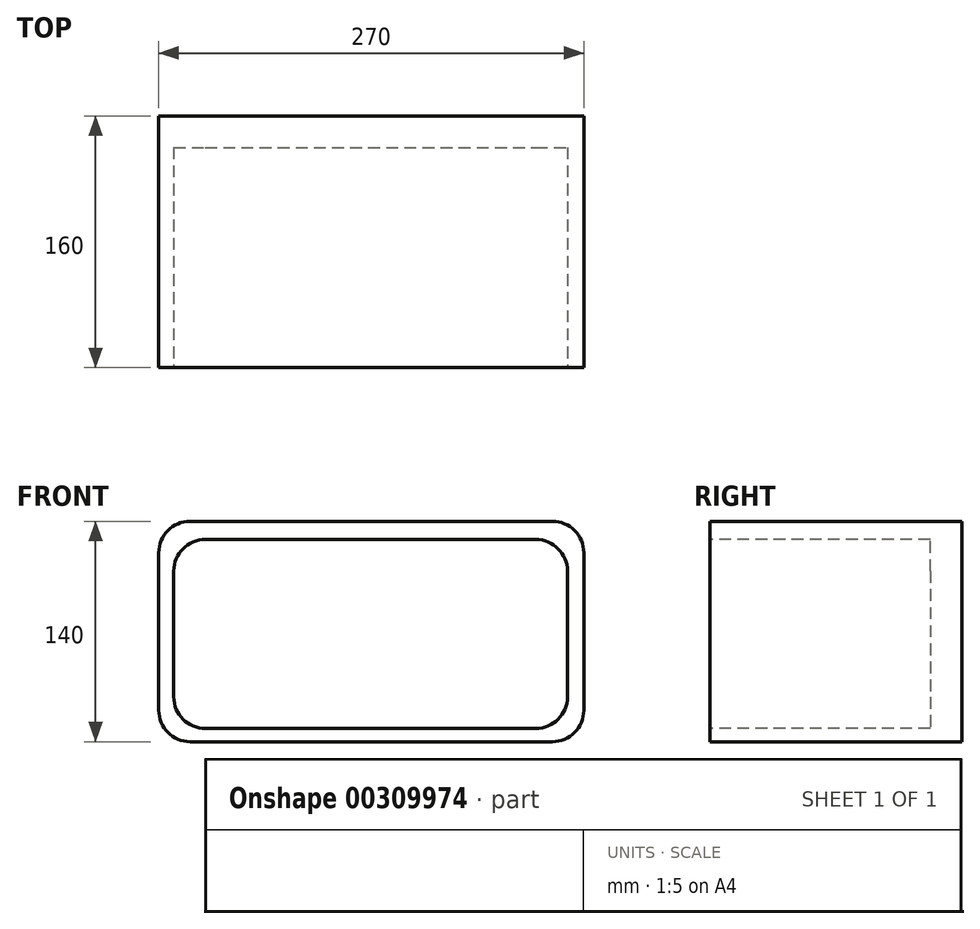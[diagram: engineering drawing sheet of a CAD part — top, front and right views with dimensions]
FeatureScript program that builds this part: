
annotation { "Feature Type Name" : "Feature", "Feature Type Description" : "" }
export const myFeature = defineFeature(function(context is Context, id is Id, definition is map)
    precondition{}
    {
        {
            var Q0;
            Q0=qCreatedBy(makeId("Front.planeOp"),FACE);
            var sketch = newSketch(context, id + "F0", { "sketchPlane" : qUnion([Q0])});
            skLineSegment(sketch, "E0.bottom", {"start": v(-135, 70) * mm, "end": v(135, 70) * mm});
            skLineSegment(sketch, "E0.top", {"start": v(-135, -70) * mm, "end": v(135, -70) * mm});
            skLineSegment(sketch, "E0.left", {"start": v(-135, 70) * mm, "end": v(-135, -70) * mm});
            skLineSegment(sketch, "E0.right", {"start": v(135, 70) * mm, "end": v(135, -70) * mm});
            skPoint(sketch, "E0.middle", {"position": v(0, 0) * mm});
            skSolve(sketch);
        }
        {
            var Q0;
            Q0 = qSketchRegion(id + "F0", true);
            extrude(context, id + "F1", {"entities" : qUnion([Q0]), "depth" : 160 * mm});
        }
        {
            var Q0;
            Q0=makeQuery(id+"F1.opExtrude","CAP_FACE",FACE,{"disambiguationData":[OSD([sQuery(id+"F0.wireOp",EDGE,"E0.bottom"),sQuery(id+"F0.wireOp",EDGE,"E0.top"),sQuery(id+"F0.wireOp",EDGE,"E0.left"),sQuery(id+"F0.wireOp",EDGE,"E0.right")])],"isStart":false});
            var sketch = newSketch(context, id + "F2", { "sketchPlane" : qUnion([Q0])});
            skLineSegment(sketch, "E1.bottom", {"start": v(-125.42, 58.4) * mm, "end": v(124.58, 58.4) * mm});
            skLineSegment(sketch, "E1.top", {"start": v(-125.42, -61.6) * mm, "end": v(124.58, -61.6) * mm});
            skLineSegment(sketch, "E1.left", {"start": v(-125.42, 58.4) * mm, "end": v(-125.42, -61.6) * mm});
            skLineSegment(sketch, "E1.right", {"start": v(124.58, 58.4) * mm, "end": v(124.58, -61.6) * mm});
            skSolve(sketch);
        }
        {
            var Q0;
            Q0 = qSketchRegion(id + "F2", true);
            extrude(context, id + "F3", {"entities" : qUnion([Q0]), "operationType" : NewBodyOperationType.REMOVE, "oppositeDirection" : true, "depth" : 140 * mm});
        }
        {
            var Q0;
            Q0=makeQuery(id+"F1.opExtrude","SWEPT_EDGE",EDGE,{"disambiguationData":[OSD([sQuery(id+"F0.wireOp",EDGE,"E0.bottom"),sQuery(id+"F0.wireOp",EDGE,"E0.right")])]});
            var Q1;
            Q1=makeQuery(id+"F1.opExtrude","SWEPT_EDGE",EDGE,{"disambiguationData":[OSD([sQuery(id+"F0.wireOp",EDGE,"E0.top"),sQuery(id+"F0.wireOp",EDGE,"E0.right")])]});
            var Q2;
            Q2=makeQuery(id+"F1.opExtrude","SWEPT_EDGE",EDGE,{"disambiguationData":[OSD([sQuery(id+"F0.wireOp",EDGE,"E0.bottom"),sQuery(id+"F0.wireOp",EDGE,"E0.left")])]});
            var Q3;
            Q3=makeQuery(id+"F1.opExtrude","SWEPT_EDGE",EDGE,{"disambiguationData":[OSD([sQuery(id+"F0.wireOp",EDGE,"E0.top"),sQuery(id+"F0.wireOp",EDGE,"E0.left")])]});
            var Q4;
            Q4=makeQuery(id+"F3.boolean.opBoolean","COPY",EDGE,{"derivedFrom":makeQuery(id+"F3.opExtrude","SWEPT_EDGE",EDGE,{"disambiguationData":[OSD([sQuery(id+"F2.wireOp",EDGE,"E1.top"),sQuery(id+"F2.wireOp",EDGE,"E1.right")])]})});
            var Q5;
            Q5=makeQuery(id+"F3.boolean.opBoolean","COPY",EDGE,{"derivedFrom":makeQuery(id+"F3.opExtrude","SWEPT_EDGE",EDGE,{"disambiguationData":[OSD([sQuery(id+"F2.wireOp",EDGE,"E1.bottom"),sQuery(id+"F2.wireOp",EDGE,"E1.right")])]})});
            var Q6;
            Q6=makeQuery(id+"F3.boolean.opBoolean","COPY",EDGE,{"derivedFrom":makeQuery(id+"F3.opExtrude","SWEPT_EDGE",EDGE,{"disambiguationData":[OSD([sQuery(id+"F2.wireOp",EDGE,"E1.bottom"),sQuery(id+"F2.wireOp",EDGE,"E1.left")])]})});
            var Q7;
            Q7=makeQuery(id+"F3.boolean.opBoolean","COPY",EDGE,{"derivedFrom":makeQuery(id+"F3.opExtrude","SWEPT_EDGE",EDGE,{"disambiguationData":[OSD([sQuery(id+"F2.wireOp",EDGE,"E1.top"),sQuery(id+"F2.wireOp",EDGE,"E1.left")])]})});
            fillet(context, id + "F4", {"entities" : qUnion([Q0, Q1, Q2, Q3, Q4, Q5, Q6, Q7]), "radius" : 20 * mm, "tangentPropagation" : true, "allowEdgeOverflow" : false});
        }
    });
